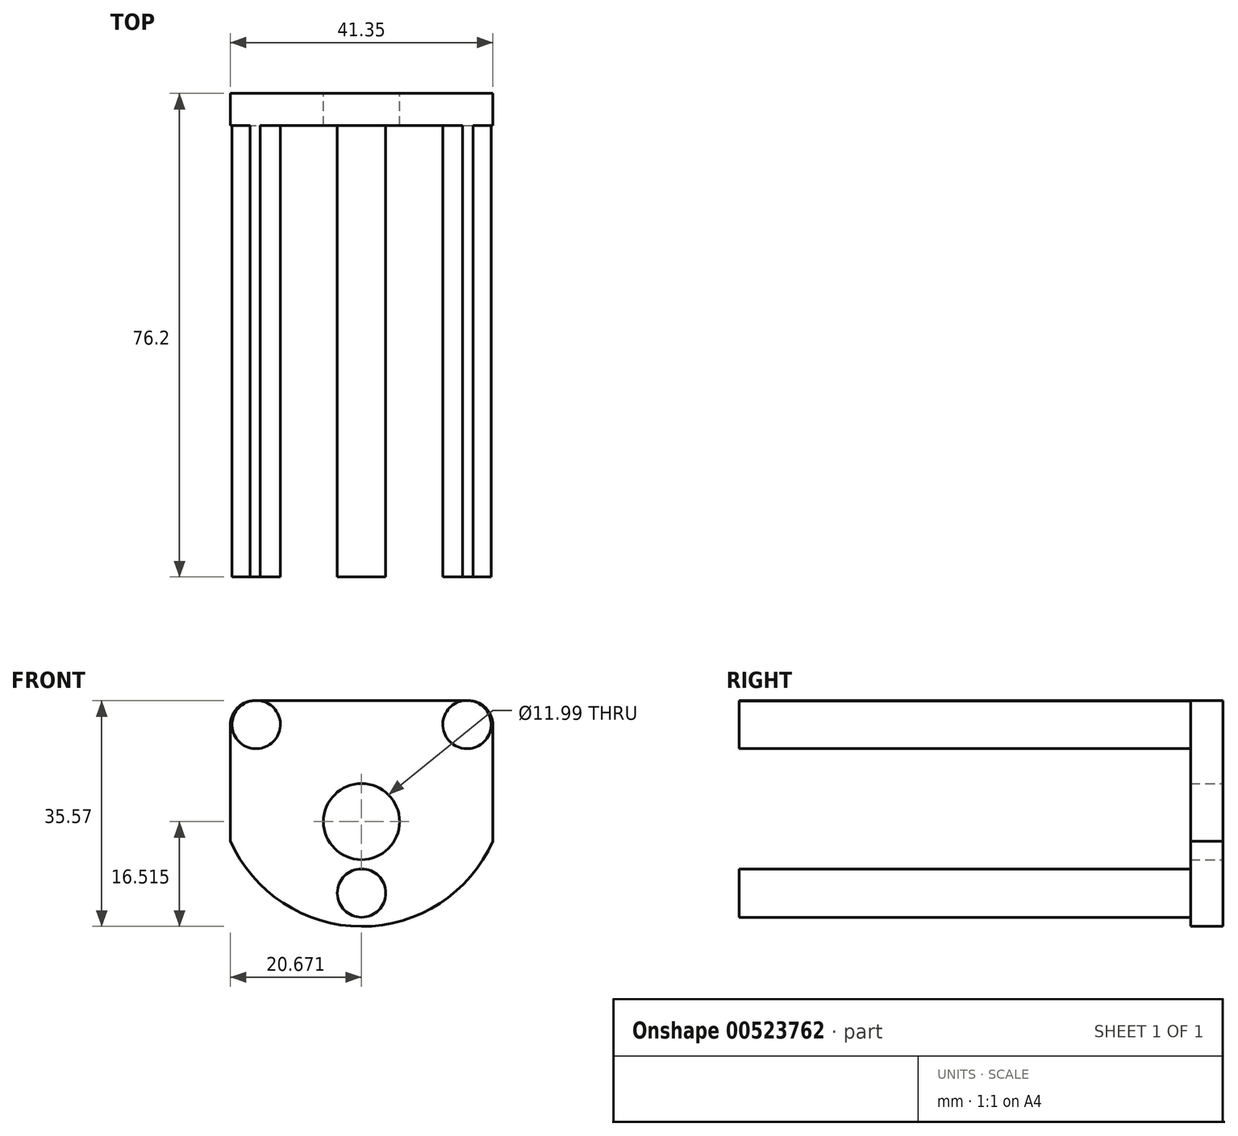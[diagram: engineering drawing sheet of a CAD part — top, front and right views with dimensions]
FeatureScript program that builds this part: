
annotation { "Feature Type Name" : "Feature", "Feature Type Description" : "" }
export const myFeature = defineFeature(function(context is Context, id is Id, definition is map)
    precondition{}
    {
        {
            var Q0;
            Q0=qCreatedBy(makeId("Front.planeOp"),FACE);
            var sketch = newSketch(context, id + "F0", { "sketchPlane" : qUnion([Q0])});
            skLineSegment(sketch, "E0.top", {"start": v(3.81, 3.89) * mm, "end": v(37.54, 3.89) * mm});
            skLineSegment(sketch, "E0.left", {"start": v(0, 0) * mm, "end": v(0, 0.08) * mm});
            skLineSegment(sketch, "E0.right", {"start": v(41.35, 0) * mm, "end": v(41.35, 0.08) * mm});
            skCircle(sketch, "E1", {"center": v(4.07, 0.13) * mm, "radius": 3.81 * mm});
            skPoint(sketch, "E1.perimeterSnap0", {"position": v(2.04, 2) * mm});
            skCircle(sketch, "E2", {"center": v(37.28, 0.13) * mm, "radius": 3.81 * mm});
            skPoint(sketch, "E3.visualSharp", {"position": v(41.35, 3.89) * mm});
            skArc(sketch, "E3.filletArc", {"start": v(41.35, 0.08) * mm, "mid": v(40.24, 2.77) * mm, "end": v(37.54, 3.89) * mm});
            skPoint(sketch, "E4.visualSharp", {"position": v(0, 3.89) * mm});
            skArc(sketch, "E4.filletArc", {"start": v(3.81, 3.89) * mm, "mid": v(1.12, 2.77) * mm, "end": v(0, 0.08) * mm});
            skCircle(sketch, "E5", {"center": v(20.67, -15.17) * mm, "radius": 6 * mm});
            skArc(sketch, "E6", {"start": v(0, 0) * mm, "mid": v(20.73, -31.68) * mm, "end": v(41.35, 0.08) * mm});
            skLineSegment(sketch, "E7", {"start": v(41.35, 0) * mm, "end": v(41.35, -18.25) * mm});
            skLineSegment(sketch, "E8", {"start": v(0, 0) * mm, "end": v(0, -18.17) * mm});
            skCircle(sketch, "E9", {"center": v(20.67, -26.42) * mm, "radius": 3.81 * mm});
            skSolve(sketch);
        }
        {
            var Q0;
            {var subQ8=sQuery(id+"F0.wireOp",EDGE,"E0.left");Q0=makeQuery(id+"F0.imprint","IMPRINT",FACE,{"disambiguationData":[TD([[makeQuery(id+"F0.imprint","IMPRINT",EDGE,{"derivedFrom":subQ8}),-1.0]])]});}
            extrude(context, id + "F1", {"entities" : qUnion([Q0]), "depth" : 5.08 * mm, "offsetDistance" : 25.4 * mm});
        }
        {
            var Q0;
            {var subQ0=sQuery(id+"F0.wireOp",EDGE,"E4.filletArc");var subQ1=sQuery(id+"F0.wireOp",EDGE,"E0.top");var subQ2=makeQuery(id+"F0.imprint","INTERSECT",VERTEX,{"derivedFrom":[subQ1,subQ0]});Q0=makeQuery(id+"F0.imprint","IMPRINT",FACE,{"disambiguationData":[TD([[makeQuery(id+"F0.imprint","IMPRINT",EDGE,{"disambiguationData":[TD([[subQ2,-1.0]])],"derivedFrom":subQ1}),-1.0]])]});}
            var Q1;
            {var subQ0=sQuery(id+"F0.wireOp",EDGE,"E3.filletArc");var subQ1=sQuery(id+"F0.wireOp",EDGE,"E0.top");var subQ2=makeQuery(id+"F0.imprint","INTERSECT",VERTEX,{"derivedFrom":[subQ1,subQ0]});Q1=makeQuery(id+"F0.imprint","IMPRINT",FACE,{"disambiguationData":[TD([[makeQuery(id+"F0.imprint","IMPRINT",EDGE,{"disambiguationData":[TD([[subQ2,1.0]])],"derivedFrom":subQ1}),-1.0]])]});}
            extrude(context, id + "F2", {"entities" : qUnion([Q0, Q1]), "operationType" : NewBodyOperationType.ADD, "depth" : 76.2 * mm, "offsetDistance" : 25.4 * mm});
        }
        {
            var Q0;
            Q0=makeQuery(id+"F0.imprint","IMPRINT",FACE,{"disambiguationData":[TD([[makeQuery(id+"F0.imprint","IMPRINT",EDGE,{"derivedFrom":sQuery(id+"F0.wireOp",EDGE,"E9")}),1.0]])]});
            extrude(context, id + "F3", {"entities" : qUnion([Q0]), "operationType" : NewBodyOperationType.ADD, "depth" : 76.2 * mm, "offsetDistance" : 25.4 * mm});
        }
    });
